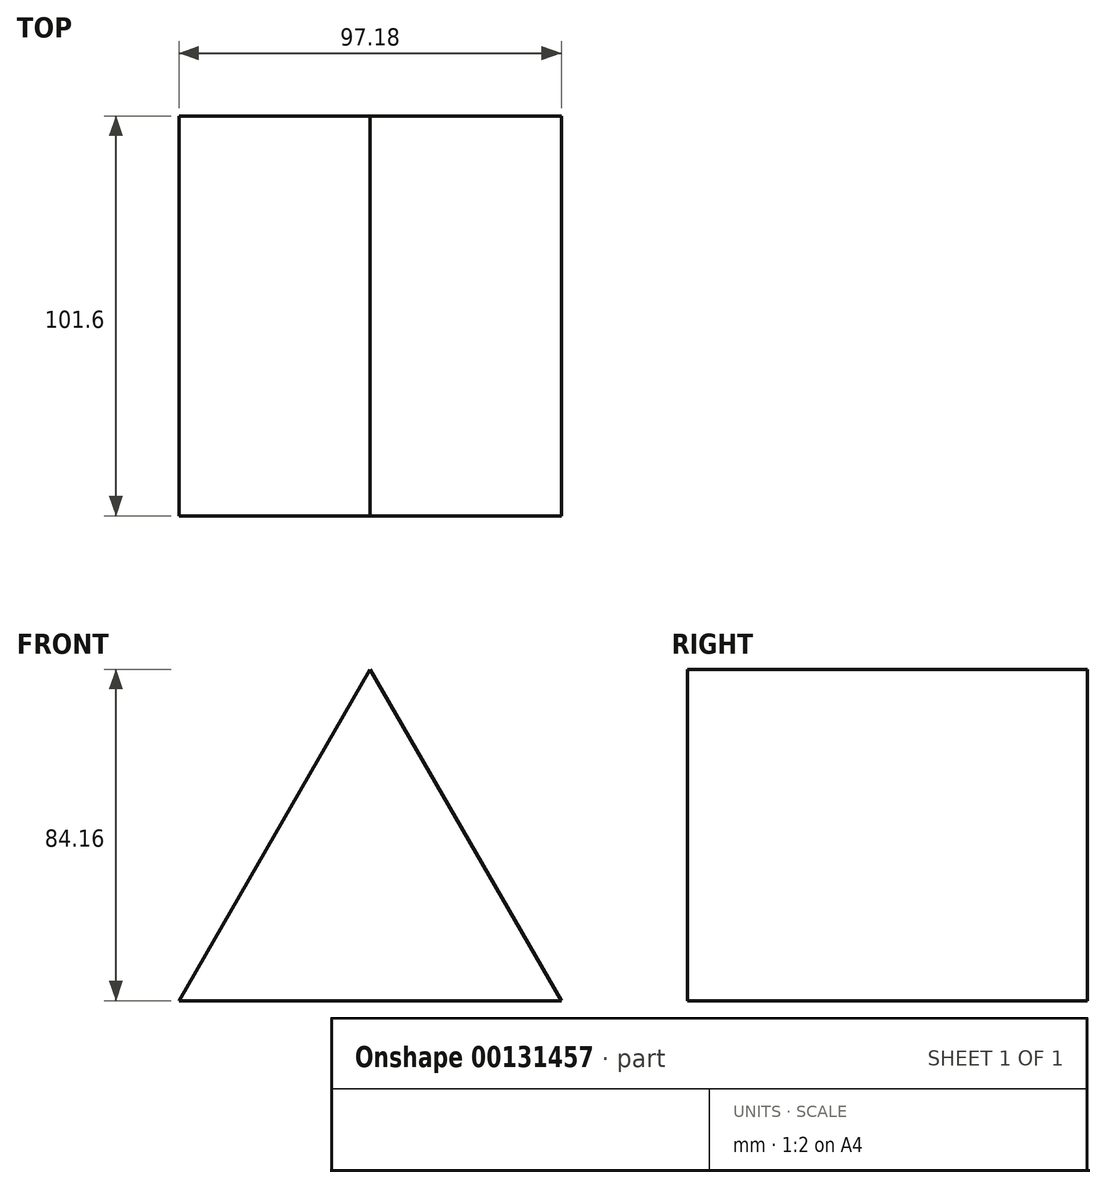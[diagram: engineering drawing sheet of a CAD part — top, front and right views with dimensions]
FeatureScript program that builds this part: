
annotation { "Feature Type Name" : "Feature", "Feature Type Description" : "" }
export const myFeature = defineFeature(function(context is Context, id is Id, definition is map)
    precondition{}
    {
        {
            var Q0;
            Q0=qCreatedBy(makeId("Front.planeOp"),FACE);
            var sketch = newSketch(context, id + "F0", { "sketchPlane" : qUnion([Q0])});
            skCircle(sketch, "E0.cCircle", {"center": v(0, 0) * mm, "radius": 56.1 * mm, "construction": true});
            skLineSegment(sketch, "E0.0", {"start": v(-48.6, -28.05) * mm, "end": v(0, 56.1) * mm});
            skLineSegment(sketch, "E0.1", {"start": v(0, 56.1) * mm, "end": v(48.6, -28.05) * mm});
            skLineSegment(sketch, "E0.2", {"start": v(48.6, -28.05) * mm, "end": v(-48.6, -28.05) * mm});
            skSolve(sketch);
        }
        {
            var Q0;
            Q0=makeQuery(id+"F0.imprint","IMPRINT",FACE,{"disambiguationData":[TD([[makeQuery(id+"F0.imprint","IMPRINT",EDGE,{"derivedFrom":sQuery(id+"F0.wireOp",EDGE,"E0.0")}),-1.0]])]});
            extrude(context, id + "F1", {"entities" : qUnion([Q0]), "depth" : 101.6 * mm});
        }
    });
